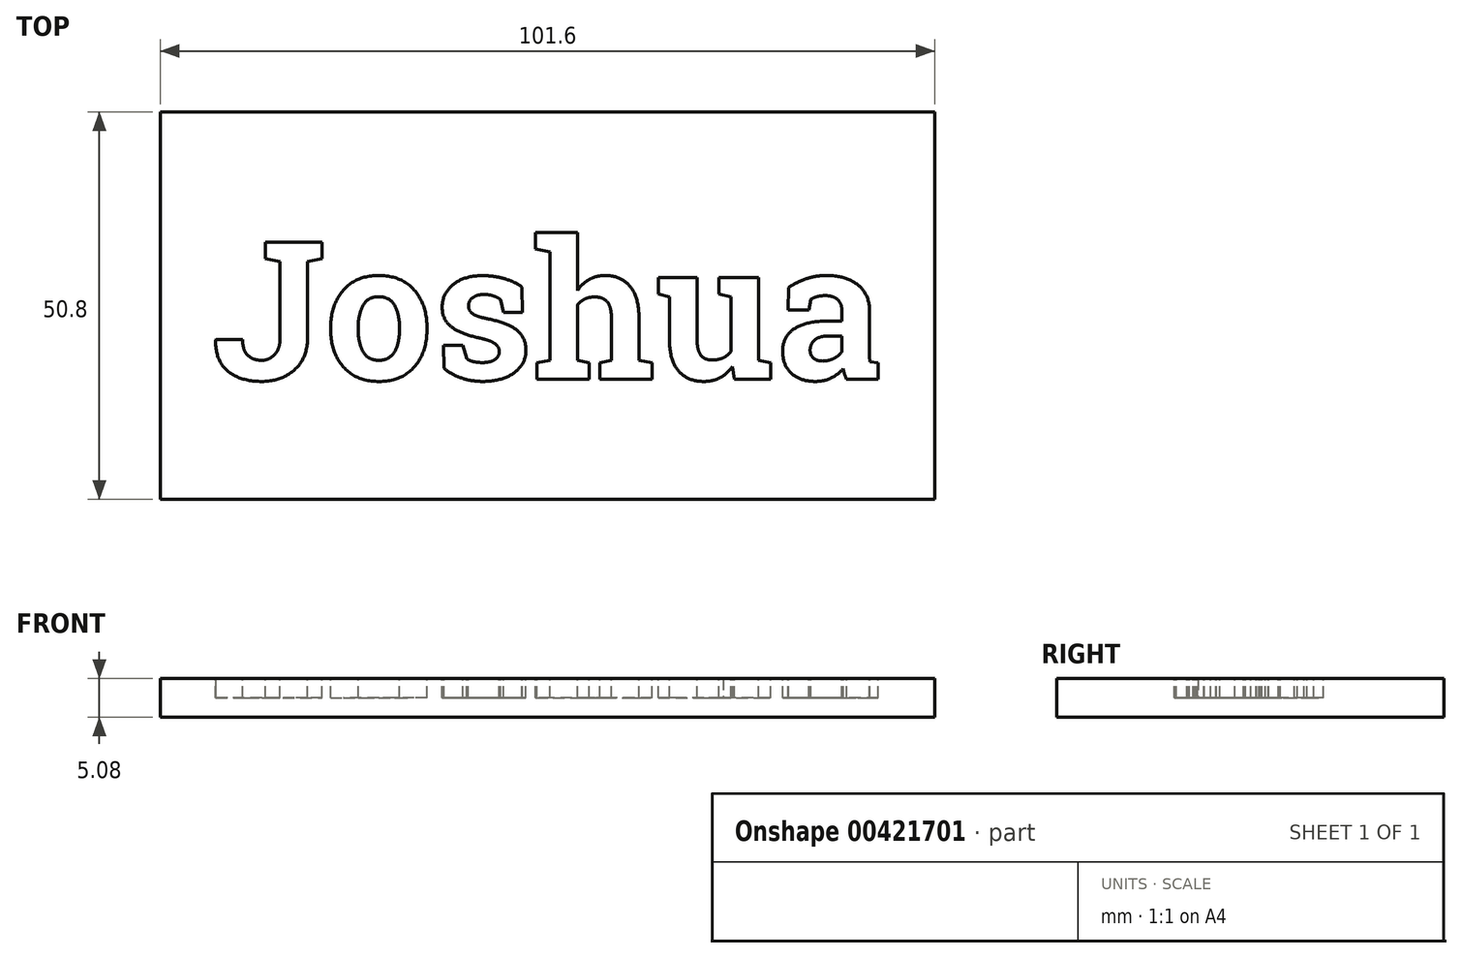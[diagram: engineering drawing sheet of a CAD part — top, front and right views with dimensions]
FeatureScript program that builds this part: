
annotation { "Feature Type Name" : "Feature", "Feature Type Description" : "" }
export const myFeature = defineFeature(function(context is Context, id is Id, definition is map)
    precondition{}
    {
        {
            var Q0;
            Q0=qCreatedBy(makeId("Top.planeOp"),FACE);
            var sketch = newSketch(context, id + "F0", { "sketchPlane" : qUnion([Q0])});
            skLineSegment(sketch, "E0.bottom", {"start": v(50.8, 25.4) * mm, "end": v(-50.8, 25.4) * mm});
            skLineSegment(sketch, "E0.top", {"start": v(50.8, -25.4) * mm, "end": v(-50.8, -25.4) * mm});
            skLineSegment(sketch, "E0.left", {"start": v(50.8, 25.4) * mm, "end": v(50.8, -25.4) * mm});
            skLineSegment(sketch, "E0.right", {"start": v(-50.8, 25.4) * mm, "end": v(-50.8, -25.4) * mm});
            skPoint(sketch, "E0.middle", {"position": v(0, 0) * mm});
            skSolve(sketch);
        }
        {
            var Q0;
            Q0=makeQuery(id+"F0.imprint","IMPRINT",FACE,{"disambiguationData":[TD([[makeQuery(id+"F0.imprint","IMPRINT",EDGE,{"derivedFrom":sQuery(id+"F0.wireOp",EDGE,"E0.bottom")}),1.0]])]});
            extrude(context, id + "F1", {"entities" : qUnion([Q0]), "depth" : 5.08 * mm});
        }
        {
            var Q0;
            Q0=makeQuery(id+"F1.opExtrude","CAP_FACE",FACE,{"disambiguationData":[OSD([sQuery(id+"F0.wireOp",EDGE,"E0.bottom"),sQuery(id+"F0.wireOp",EDGE,"E0.top"),sQuery(id+"F0.wireOp",EDGE,"E0.left"),sQuery(id+"F0.wireOp",EDGE,"E0.right")])],"isStart":false});
            var sketch = newSketch(context, id + "F2", { "sketchPlane" : qUnion([Q0])});
            skText(sketch, "E1", { "text": "Joshua", "fontName": "RobotoSlab-Bold.ttf"});
            const initialGuessF2  = {"E1": [-0.04398, -0.00969, 1, 0, 0.01824]};
            skSetInitialGuess(sketch, initialGuessF2);
            skSolve(sketch);
        }
        {
            var Q0;
            Q0 = qSketchRegion(id + "F2", true);
            extrude(context, id + "F3", {"entities" : qUnion([Q0]), "operationType" : NewBodyOperationType.REMOVE, "oppositeDirection" : true, "depth" : 2.54 * mm});
        }
    });
